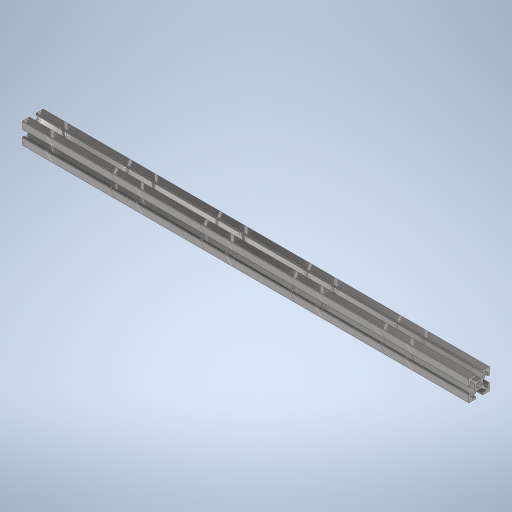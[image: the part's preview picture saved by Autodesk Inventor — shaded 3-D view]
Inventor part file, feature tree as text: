
AUTODESK INVENTOR PART (.ipt)
format: ipt  version: 2023 (Build 270158000, 158)  size: 402,944 bytes
history: native  units: mm
features: extrude x1, sketch x1
ambient origin geometry x8: Origin, YZ Plane, XZ Plane, XY Plane, X Axis, Y Axis, Z Axis, Center Point
bodies: Solide1 (feature_tree)
feature tree (2):
  extrude  "Extrusion1"  Depth=10.0mm
  sketch  "Esquisse1"
